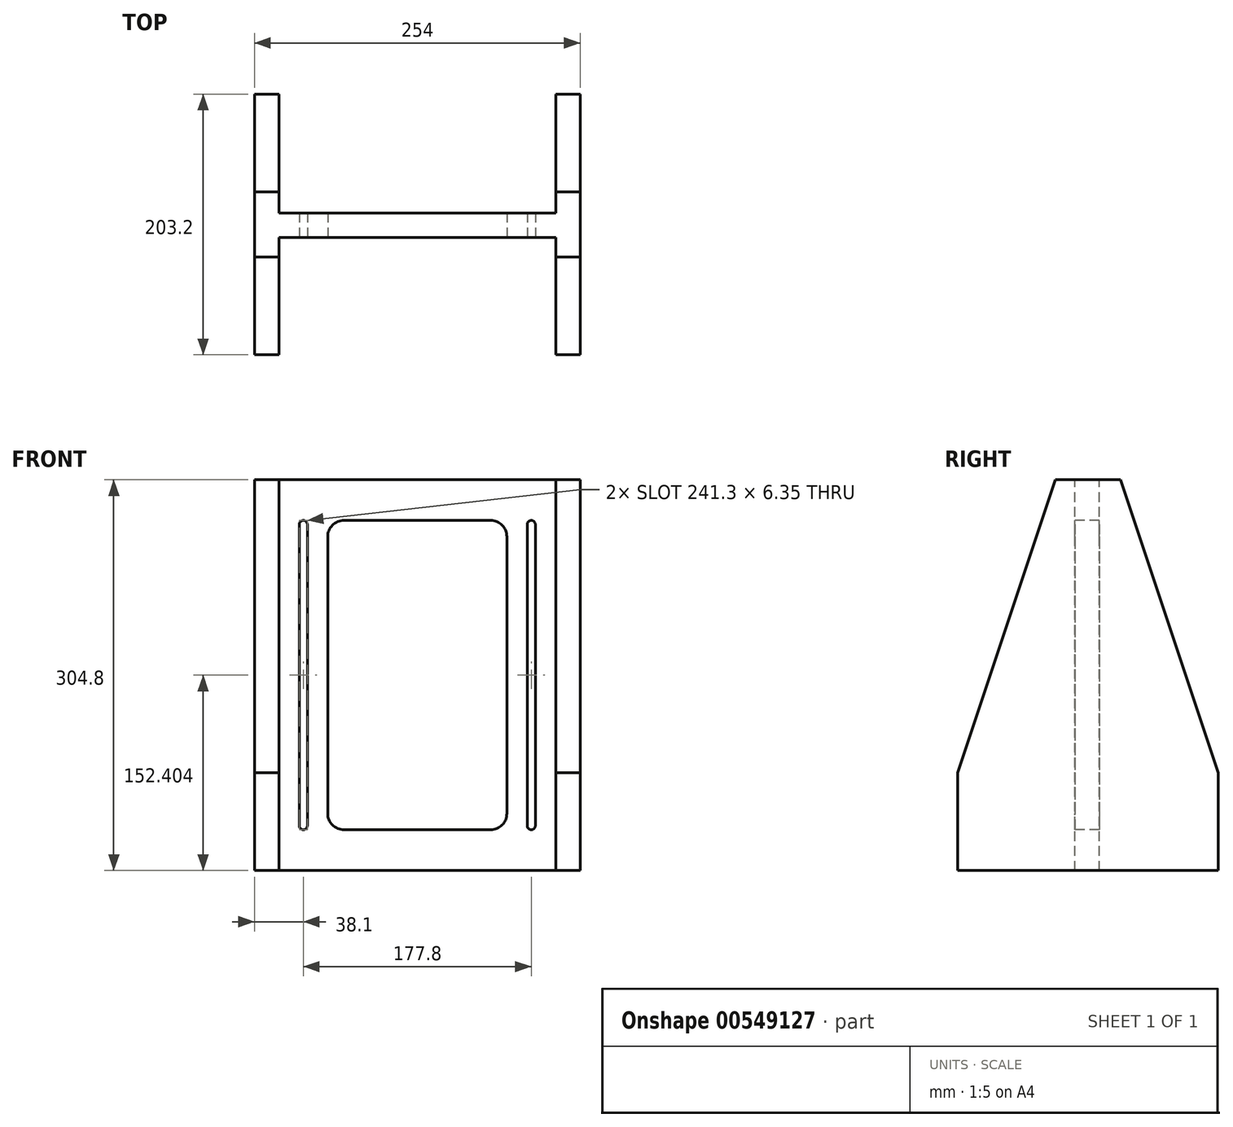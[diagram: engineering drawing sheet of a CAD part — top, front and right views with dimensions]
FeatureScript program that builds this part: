
annotation { "Feature Type Name" : "Feature", "Feature Type Description" : "" }
export const myFeature = defineFeature(function(context is Context, id is Id, definition is map)
    precondition{}
    {
        {
            var Q0;
            Q0=qCreatedBy(makeId("Right.planeOp"),FACE);
            var sketch = newSketch(context, id + "F0", { "sketchPlane" : qUnion([Q0])});
            skLineSegment(sketch, "E0", {"start": v(-24.83, 119.26) * mm, "end": v(-101.03, -109.34) * mm});
            skLineSegment(sketch, "E1", {"start": v(-101.03, -109.34) * mm, "end": v(-101.03, -185.54) * mm});
            skLineSegment(sketch, "E2", {"start": v(-101.03, -185.54) * mm, "end": v(102.17, -185.54) * mm});
            skLineSegment(sketch, "E3", {"start": v(102.17, -185.54) * mm, "end": v(102.17, -109.34) * mm});
            skLineSegment(sketch, "E4", {"start": v(102.17, -109.34) * mm, "end": v(25.97, 119.26) * mm});
            skLineSegment(sketch, "E5", {"start": v(25.97, 119.26) * mm, "end": v(-24.83, 119.26) * mm});
            skLineSegment(sketch, "E6", {"start": v(0.57, 119.26) * mm, "end": v(0.57, -185.54) * mm, "construction": true});
            skSolve(sketch);
        }
        {
            var Q0;
            Q0 = qSketchRegion(id + "F0", true);
            extrude(context, id + "F1", {"entities" : qUnion([Q0]), "depth" : 254 * mm, "offsetDistance" : 25.4 * mm});
        }
        {
            var Q0;
            Q0=makeQuery(id+"F1.opExtrude","SWEPT_FACE",FACE,{"disambiguationData":[OSD([sQuery(id+"F0.wireOp",EDGE,"E5")])]});
            var sketch = newSketch(context, id + "F2", { "sketchPlane" : qUnion([Q0])});
            skLineSegment(sketch, "E7.bottom", {"start": v(19.05, 102.17) * mm, "end": v(234.95, 102.17) * mm});
            skLineSegment(sketch, "E7.top", {"start": v(19.05, 9.52) * mm, "end": v(234.95, 9.53) * mm});
            skLineSegment(sketch, "E7.left", {"start": v(19.05, 102.17) * mm, "end": v(19.05, 9.52) * mm});
            skLineSegment(sketch, "E7.right", {"start": v(234.95, 102.17) * mm, "end": v(234.95, 9.53) * mm});
            skLineSegment(sketch, "E8.bottom", {"start": v(19.05, -101.03) * mm, "end": v(234.95, -101.03) * mm});
            skLineSegment(sketch, "E8.top", {"start": v(19.05, -9.53) * mm, "end": v(234.95, -9.52) * mm});
            skLineSegment(sketch, "E8.left", {"start": v(19.05, -101.03) * mm, "end": v(19.05, -9.53) * mm});
            skLineSegment(sketch, "E8.right", {"start": v(234.95, -101.03) * mm, "end": v(234.95, -9.52) * mm});
            skLineSegment(sketch, "E9", {"start": v(254, 0) * mm, "end": v(0, 0) * mm, "construction": true});
            skPoint(sketch, "E9.startSnap0", {"position": v(254, 0.57) * mm});
            skSolve(sketch);
        }
        {
            var Q0;
            Q0 = qSketchRegion(id + "F2", true);
            extrude(context, id + "F3", {"entities" : qUnion([Q0]), "operationType" : NewBodyOperationType.REMOVE, "endBound" : BoundingType.THROUGH_ALL, "oppositeDirection" : true, "depth" : 25.4 * mm, "offsetDistance" : 25.4 * mm});
        }
        {
            var Q0;
            Q0=makeQuery(id+"F3.boolean.opBoolean","COPY",FACE,{"derivedFrom":makeQuery(id+"F3.opExtrude","SWEPT_FACE",FACE,{"disambiguationData":[OSD([sQuery(id+"F2.wireOp",EDGE,"E8.top")])]})});
            var sketch = newSketch(context, id + "F4", { "sketchPlane" : qUnion([Q0])});
            skLineSegment(sketch, "E10.bottom", {"start": v(69.85, 87.51) * mm, "end": v(184.15, 87.51) * mm});
            skLineSegment(sketch, "E10.top", {"start": v(69.85, -153.79) * mm, "end": v(184.15, -153.79) * mm});
            skLineSegment(sketch, "E10.left", {"start": v(57.15, 74.81) * mm, "end": v(57.15, -141.09) * mm});
            skLineSegment(sketch, "E10.right", {"start": v(196.85, 74.81) * mm, "end": v(196.85, -141.09) * mm});
            skPoint(sketch, "E11.visualSharp", {"position": v(57.15, 87.51) * mm});
            skArc(sketch, "E11.filletArc", {"start": v(69.85, 87.51) * mm, "mid": v(60.87, 83.8) * mm, "end": v(57.15, 74.81) * mm});
            skPoint(sketch, "E12.visualSharp", {"position": v(196.85, 87.51) * mm});
            skArc(sketch, "E12.filletArc", {"start": v(196.85, 74.81) * mm, "mid": v(193.13, 83.8) * mm, "end": v(184.15, 87.51) * mm});
            skPoint(sketch, "E13.visualSharp", {"position": v(196.85, -153.79) * mm});
            skArc(sketch, "E13.filletArc", {"start": v(184.15, -153.79) * mm, "mid": v(193.13, -150.07) * mm, "end": v(196.85, -141.09) * mm});
            skPoint(sketch, "E14.visualSharp", {"position": v(57.15, -153.79) * mm});
            skArc(sketch, "E14.filletArc", {"start": v(57.15, -141.09) * mm, "mid": v(60.87, -150.07) * mm, "end": v(69.85, -153.79) * mm});
            skSolve(sketch);
        }
        {
            var Q0;
            Q0 = qSketchRegion(id + "F4", true);
            extrude(context, id + "F5", {"entities" : qUnion([Q0]), "operationType" : NewBodyOperationType.REMOVE, "endBound" : BoundingType.THROUGH_ALL, "oppositeDirection" : true, "depth" : 25.4 * mm, "offsetDistance" : 25.4 * mm});
        }
        {
            var Q0;
            Q0=makeQuery(id+"F3.boolean.opBoolean","COPY",FACE,{"derivedFrom":makeQuery(id+"F3.opExtrude","SWEPT_FACE",FACE,{"disambiguationData":[OSD([sQuery(id+"F2.wireOp",EDGE,"E8.top")])]})});
            var sketch = newSketch(context, id + "F6", { "sketchPlane" : qUnion([Q0])});
            skLineSegment(sketch, "E15.bottom", {"start": v(38.1, 87.51) * mm, "end": v(38.1, 87.51) * mm});
            skLineSegment(sketch, "E15.top", {"start": v(38.1, -153.79) * mm, "end": v(38.1, -153.79) * mm});
            skLineSegment(sketch, "E15.left", {"start": v(34.92, 84.34) * mm, "end": v(34.93, -150.61) * mm});
            skLineSegment(sketch, "E15.right", {"start": v(41.27, 84.34) * mm, "end": v(41.27, -150.61) * mm});
            skLineSegment(sketch, "E16", {"start": v(38.1, 119.26) * mm, "end": v(38.1, -185.54) * mm, "construction": true});
            skLineSegment(sketch, "E17", {"start": v(127, 119.26) * mm, "end": v(127, -185.54) * mm, "construction": true});
            skPoint(sketch, "E18.visualSharp", {"position": v(41.27, 87.51) * mm});
            skArc(sketch, "E18.filletArc", {"start": v(41.27, 84.34) * mm, "mid": v(40.35, 86.58) * mm, "end": v(38.1, 87.51) * mm});
            skPoint(sketch, "E19.visualSharp", {"position": v(34.92, 87.51) * mm});
            skArc(sketch, "E19.filletArc", {"start": v(38.1, 87.51) * mm, "mid": v(35.85, 86.58) * mm, "end": v(34.92, 84.34) * mm});
            skPoint(sketch, "E20.visualSharp", {"position": v(41.27, -153.79) * mm});
            skArc(sketch, "E20.filletArc", {"start": v(38.1, -153.79) * mm, "mid": v(40.35, -152.86) * mm, "end": v(41.27, -150.61) * mm});
            skPoint(sketch, "E21.visualSharp", {"position": v(34.93, -153.79) * mm});
            skArc(sketch, "E21.filletArc", {"start": v(34.93, -150.61) * mm, "mid": v(35.85, -152.86) * mm, "end": v(38.1, -153.79) * mm});
            skArc(sketch, "E22.MirrorCS", {"start": v(219.08, -150.61) * mm, "mid": v(218.15, -152.86) * mm, "end": v(215.9, -153.79) * mm});
            skArc(sketch, "E23.MirrorCS", {"start": v(212.72, 84.34) * mm, "mid": v(213.65, 86.58) * mm, "end": v(215.9, 87.51) * mm});
            skArc(sketch, "E24.MirrorCS", {"start": v(215.9, 87.51) * mm, "mid": v(218.15, 86.58) * mm, "end": v(219.07, 84.34) * mm});
            skArc(sketch, "E25.MirrorCS", {"start": v(215.9, -153.79) * mm, "mid": v(213.65, -152.86) * mm, "end": v(212.73, -150.61) * mm});
            skPoint(sketch, "E26.MirrorP", {"position": v(219.08, 87.51) * mm});
            skLineSegment(sketch, "E27.MirrorCS", {"start": v(215.9, 87.51) * mm, "end": v(215.9, 87.51) * mm});
            skLineSegment(sketch, "E28.MirrorCS", {"start": v(215.9, 119.26) * mm, "end": v(215.9, -185.54) * mm, "construction": true});
            skLineSegment(sketch, "E29.MirrorCS", {"start": v(212.73, 84.34) * mm, "end": v(212.73, -150.61) * mm});
            skLineSegment(sketch, "E30.MirrorCS", {"start": v(219.08, 84.34) * mm, "end": v(219.08, -150.61) * mm});
            skPoint(sketch, "E31.MirrorP", {"position": v(212.73, -153.79) * mm});
            skPoint(sketch, "E32.MirrorP", {"position": v(219.08, -153.79) * mm});
            skPoint(sketch, "E33.MirrorP", {"position": v(212.73, 87.51) * mm});
            skLineSegment(sketch, "E34.MirrorCS", {"start": v(215.9, -153.79) * mm, "end": v(215.9, -153.79) * mm});
            skSolve(sketch);
        }
        {
            var Q0;
            Q0 = qSketchRegion(id + "F6", true);
            extrude(context, id + "F7", {"entities" : qUnion([Q0]), "operationType" : NewBodyOperationType.REMOVE, "endBound" : BoundingType.THROUGH_ALL, "oppositeDirection" : true, "depth" : 25.4 * mm, "offsetDistance" : 25.4 * mm});
        }
    });
